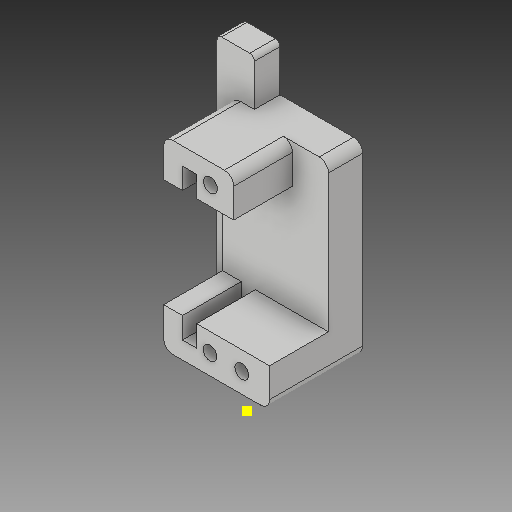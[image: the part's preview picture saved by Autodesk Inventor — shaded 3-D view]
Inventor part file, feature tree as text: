
AUTODESK INVENTOR PART (.ipt)
format: ipt  version: 2018 (Build 220112000, 112)  size: 239,104 bytes
history: native  units: mm
features: reference x12, sketch x7, other x7, extrude x6, plane x4, fillet x3, projected_geometry x2
ambient origin geometry x8: Origin, YZ Plane, XZ Plane, XY Plane, X Axis, Y Axis, Z Axis, Center Point
bodies: Solid1 (feature_tree)
feature tree (41):
  sketch  "Sketch1"  dims[d0=1.0mm d1=40.0mm]
  plane  "Work Plane1"
  extrude  "Extrusion1"  Depth=40.0mm
  sketch  "Sketch2"  dims[d2=0.0mm d3=30.0mm]
  plane  "Work Plane2"
  extrude  "Extrusion2"  Depth=30.0mm
  extrude  "Extrusion3"  TaperAngle=0.0deg  [1 undecoded]
  fillet  "Fillet1"  Radius=10.0mm
  sketch  "Sketch4"  dims[d9=4.0mm d10=4.0mm]
  sketch  "Sketch5"  dims[d11=3.25mm d12=5.0mm d13=0.0mm d14=2.0mm]
  plane  "Work Plane3"
  extrude  "Extrusion4"  Depth=4.0mm
  extrude  "Extrusion5"  Depth=5.0mm TaperAngle=0.0deg
  fillet  "Fillet2"  Radius=2.0mm
  sketch  "Sketch7"  dims[d25=3.0mm d26=3.0mm d27=7.0mm d28=0.0mm d29=2.0mm d30=3.1mm d32=10.0mm d33=0.0mm d36=1.0mm d39=50.0mm d40=5.0mm]
  plane  "Work Plane4"
  extrude  "Extrusion6"  Depth=5.0mm TaperAngle=0.0deg
  fillet  "Fillet3"  Radius=3.0mm
  reference  "Reference1"
  reference  "Reference2"
  reference  "Reference3"
  projected_geometry  "Projected Loop1"
  sketch  "Sketch3"  dims[d4=0.0mm d5=0.0mm d6=0.0mm d7=10.0mm d8=0.0mm]
  reference  "Reference4"
  reference  "Reference5"
  reference  "Reference6"
  reference  "Reference7"
  reference  "Reference8"
  reference  "Reference9"
  sketch  "Sketch6"  dims[d21=2.0mm d22=5.0mm d23=0.0mm d24=3.0mm]
  reference  "Reference10"
  reference  "Reference11"
  reference  "Reference12"
  projected_geometry  "Projected Loop2"
  other  "<userpath>\OneDrive\Documents\Inventor\TSA\2018\Animatronics\Tortoise\Turtle3.iam"
  other  "Turtle3.iam"
  other  "ButtonMountLegs:2"
  other  "servo (2):8"
  other  "SyringeServoBaseClamp:1"
  other  "SyringeServoBaseClamp:2"
  other  "HeadOpenRack:1"
note: 1 required parameter value undecoded (feature->parameter linkage not recoverable at this tier; creation-order binding heuristic only, values carry confidence <= 0.55)
